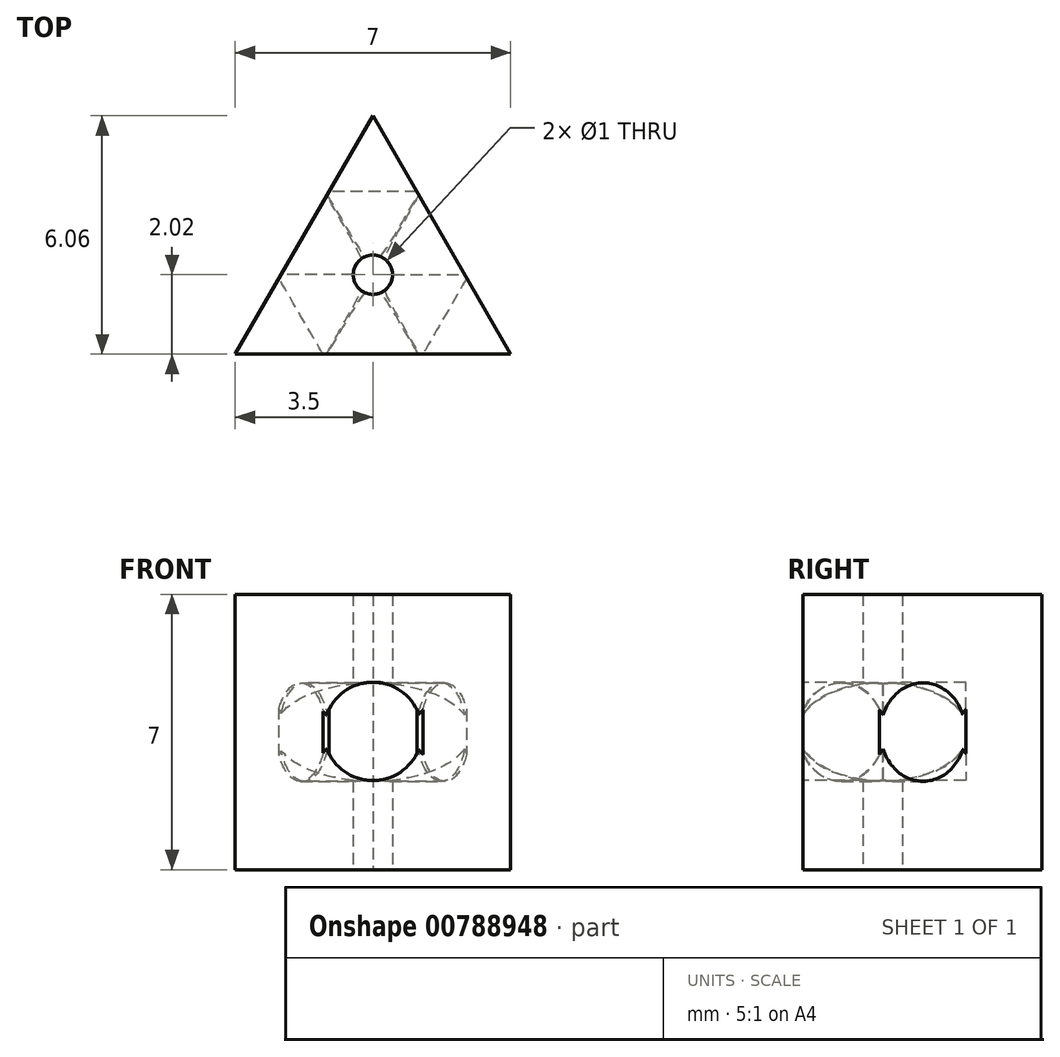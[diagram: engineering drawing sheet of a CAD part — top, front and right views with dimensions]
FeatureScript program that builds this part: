
annotation { "Feature Type Name" : "Feature", "Feature Type Description" : "" }
export const myFeature = defineFeature(function(context is Context, id is Id, definition is map)
    precondition{}
    {
        {
            var Q0;
            Q0=qCreatedBy(makeId("Top.planeOp"),FACE);
            var sketch = newSketch(context, id + "F0", { "sketchPlane" : qUnion([Q0])});
            skLineSegment(sketch, "E0", {"start": v(-20.07, -21.9) * mm, "end": v(-13.07, -21.9) * mm});
            skLineSegment(sketch, "E1", {"start": v(-13.07, -21.9) * mm, "end": v(-16.57, -15.84) * mm});
            skLineSegment(sketch, "E2", {"start": v(-16.57, -15.84) * mm, "end": v(-20.07, -21.9) * mm});
            skSolve(sketch);
        }
        {
            var Q0;
            Q0=makeQuery(id+"F0.imprint","IMPRINT",FACE,{"disambiguationData":[TD([[makeQuery(id+"F0.imprint","IMPRINT",EDGE,{"derivedFrom":sQuery(id+"F0.wireOp",EDGE,"E0")}),1.0]])]});
            extrude(context, id + "F1", {"entities" : qUnion([Q0]), "depth" : 7 * mm, "offsetDistance" : 25 * mm});
        }
        {
            var Q0;
            Q0=makeQuery(id+"F1.opExtrude","SWEPT_FACE",FACE,{"disambiguationData":[OSD([sQuery(id+"F0.wireOp",EDGE,"E1")])]});
            var sketch = newSketch(context, id + "F2", { "sketchPlane" : qUnion([Q0])});
            skCircle(sketch, "E3", {"center": v(-8.91, 3.5) * mm, "radius": 3.5 * mm});
            skPoint(sketch, "E3.first.point", {"position": v(-8.93, 7) * mm});
            skPoint(sketch, "E3.second.point", {"position": v(-8.93, 0) * mm});
            skPoint(sketch, "E3.third.point", {"position": v(-5.43, 3.84) * mm});
            skCircle(sketch, "E4", {"center": v(-8.91, 3.5) * mm, "radius": 1.25 * mm});
            skSolve(sketch);
        }
        {
            var Q0;
            Q0=makeQuery(id+"F1.opExtrude","SWEPT_FACE",FACE,{"disambiguationData":[OSD([sQuery(id+"F0.wireOp",EDGE,"E2")])]});
            var sketch = newSketch(context, id + "F3", { "sketchPlane" : qUnion([Q0])});
            skCircle(sketch, "E5", {"center": v(25.5, 3.5) * mm, "radius": 3.5 * mm});
            skPoint(sketch, "E5.first.point", {"position": v(22, 3.5) * mm});
            skPoint(sketch, "E5.second.point", {"position": v(29, 3.5) * mm});
            skPoint(sketch, "E5.third.point", {"position": v(25.5, 7) * mm});
            skCircle(sketch, "E6", {"center": v(25.5, 3.5) * mm, "radius": 1.25 * mm});
            skSolve(sketch);
        }
        {
            var Q0;
            Q0=makeQuery(id+"F1.opExtrude","SWEPT_FACE",FACE,{"disambiguationData":[OSD([sQuery(id+"F0.wireOp",EDGE,"E0")])]});
            var sketch = newSketch(context, id + "F4", { "sketchPlane" : qUnion([Q0])});
            skCircle(sketch, "E7", {"center": v(-16.57, 3.52) * mm, "radius": 3.5 * mm});
            skPoint(sketch, "E7.first.point", {"position": v(-20.07, 3.5) * mm});
            skPoint(sketch, "E7.second.point", {"position": v(-13.07, 3.5) * mm});
            skPoint(sketch, "E7.third.point", {"position": v(-16.91, 7) * mm});
            skCircle(sketch, "E8", {"center": v(-16.57, 3.52) * mm, "radius": 1.25 * mm});
            skSolve(sketch);
        }
        {
            var Q0;
            Q0=makeQuery(id+"F4.imprint","IMPRINT",FACE,{"disambiguationData":[TD([[makeQuery(id+"F4.imprint","IMPRINT",EDGE,{"derivedFrom":sQuery(id+"F4.wireOp",EDGE,"E8")}),1.0]])]});
            extrude(context, id + "F5", {"entities" : qUnion([Q0]), "operationType" : NewBodyOperationType.REMOVE, "oppositeDirection" : true, "depth" : 4.13 * mm, "offsetDistance" : 25 * mm});
        }
        {
            var Q0;
            Q0=makeQuery(id+"F2.imprint","IMPRINT",FACE,{"disambiguationData":[TD([[makeQuery(id+"F2.imprint","IMPRINT",EDGE,{"derivedFrom":sQuery(id+"F2.wireOp",EDGE,"E4")}),1.0]])]});
            extrude(context, id + "F6", {"entities" : qUnion([Q0]), "operationType" : NewBodyOperationType.REMOVE, "oppositeDirection" : true, "depth" : 4.13 * mm, "offsetDistance" : 25 * mm});
        }
        {
            var Q0;
            Q0=makeQuery(id+"F3.imprint","IMPRINT",FACE,{"disambiguationData":[TD([[makeQuery(id+"F3.imprint","IMPRINT",EDGE,{"derivedFrom":sQuery(id+"F3.wireOp",EDGE,"E6")}),1.0]])]});
            var Q1;
            Q1=sQuery(id+"F3.wireOp",EDGE,"E6");
            extrude(context, id + "F7", {"entities" : qUnion([Q0]), "operationType" : NewBodyOperationType.REMOVE, "surfaceEntities" : qUnion([Q1]), "oppositeDirection" : true, "depth" : 4.13 * mm, "offsetDistance" : 25 * mm});
        }
        {
            var Q0;
            Q0=makeQuery(id+"F1.opExtrude","CAP_FACE",FACE,{"disambiguationData":[OSD([sQuery(id+"F0.wireOp",EDGE,"E0"),sQuery(id+"F0.wireOp",EDGE,"E1"),sQuery(id+"F0.wireOp",EDGE,"E2")])],"isStart":true});
            var sketch = newSketch(context, id + "F8", { "sketchPlane" : qUnion([Q0])});
            skCircle(sketch, "E9", {"center": v(-16.57, 19.88) * mm, "radius": 4.04 * mm});
            skPoint(sketch, "E9.first.point", {"position": v(-16.57, 15.84) * mm});
            skPoint(sketch, "E9.second.point", {"position": v(-20.07, 21.9) * mm});
            skPoint(sketch, "E9.third.point", {"position": v(-13.07, 21.9) * mm});
            skCircle(sketch, "E10", {"center": v(-16.57, 19.88) * mm, "radius": 0.5 * mm});
            skSolve(sketch);
        }
        {
            var Q0;
            Q0=makeQuery(id+"F8.imprint","IMPRINT",FACE,{"disambiguationData":[TD([[makeQuery(id+"F8.imprint","IMPRINT",EDGE,{"derivedFrom":sQuery(id+"F8.wireOp",EDGE,"E10")}),1.0]])]});
            var Q1;
            Q1=sQuery(id+"F8.wireOp",EDGE,"E10");
            extrude(context, id + "F9", {"entities" : qUnion([Q0]), "operationType" : NewBodyOperationType.REMOVE, "surfaceEntities" : qUnion([Q1]), "oppositeDirection" : true, "depth" : 25 * mm, "offsetDistance" : 25 * mm});
        }
    });
